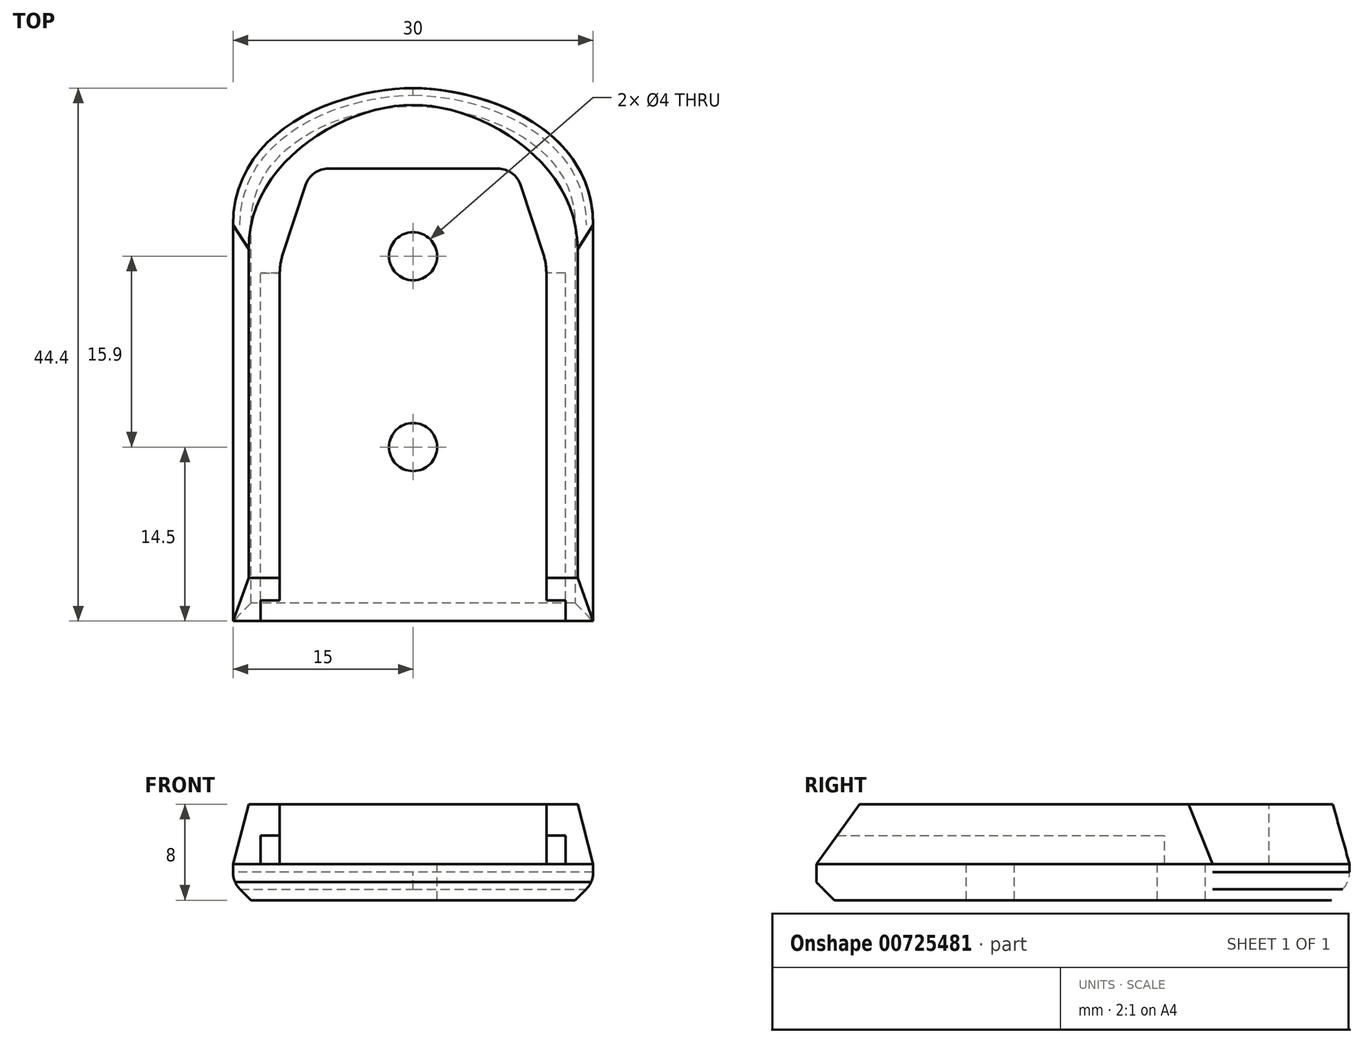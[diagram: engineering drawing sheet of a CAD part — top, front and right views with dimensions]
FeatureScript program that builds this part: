
annotation { "Feature Type Name" : "Feature", "Feature Type Description" : "" }
export const myFeature = defineFeature(function(context is Context, id is Id, definition is map)
    precondition{}
    {
        {
            var Q0;
            Q0=qCreatedBy(makeId("Top.planeOp"),FACE);
            var sketch = newSketch(context, id + "F0", { "sketchPlane" : qUnion([Q0])});
            skLineSegment(sketch, "E0", {"start": v(-15, 0) * mm, "end": v(-15, 33) * mm});
            skFitSpline(sketch, "E1", {"points": [v(-15, 33) * mm, v(0, 44.4) * mm], "startDerivative": vector(0, 25.02) * mm, "endDerivative": vector(16.53, 0) * mm});
            skLineSegment(sketch, "E2", {"start": v(0, 0) * mm, "end": v(-15, 0) * mm});
            skLineSegment(sketch, "E3.MirrorCS", {"start": v(15, 0) * mm, "end": v(15, 33) * mm});
            skLineSegment(sketch, "E4.MirrorCS", {"start": v(0, 0) * mm, "end": v(15, 0) * mm});
            skFitSpline(sketch, "E5.MirrorCS", {"points": [v(15, 33) * mm, v(0, 44.4) * mm], "startDerivative": vector(0, 25.02) * mm, "endDerivative": vector(-16.53, 0) * mm});
            skPoint(sketch, "E6", {"position": v(0, 14.5) * mm});
            skPoint(sketch, "E7", {"position": v(0, 30.4) * mm});
            skLineSegment(sketch, "E8", {"start": v(-11.1, 0) * mm, "end": v(-11.1, 29) * mm});
            skLineSegment(sketch, "E9", {"start": v(-10.85, 30.56) * mm, "end": v(-8.95, 36.33) * mm});
            skLineSegment(sketch, "E10", {"start": v(-7.05, 37.7) * mm, "end": v(0, 37.7) * mm});
            skPoint(sketch, "E11.visualSharp", {"position": v(-11.1, 29.8) * mm});
            skArc(sketch, "E11.filletArc", {"start": v(-10.85, 30.56) * mm, "mid": v(-11.04, 29.8) * mm, "end": v(-11.1, 29) * mm});
            skPoint(sketch, "E12.visualSharp", {"position": v(-8.5, 37.7) * mm});
            skArc(sketch, "E12.filletArc", {"start": v(-7.05, 37.7) * mm, "mid": v(-8.23, 37.32) * mm, "end": v(-8.95, 36.33) * mm});
            skLineSegment(sketch, "E13.MirrorCS", {"start": v(7.05, 37.7) * mm, "end": v(0, 37.7) * mm});
            skArc(sketch, "E14.MirrorCS", {"start": v(7.05, 37.7) * mm, "mid": v(8.23, 37.32) * mm, "end": v(8.95, 36.33) * mm});
            skLineSegment(sketch, "E15.MirrorCS", {"start": v(10.85, 30.56) * mm, "end": v(8.95, 36.33) * mm});
            skArc(sketch, "E16.MirrorCS", {"start": v(10.85, 30.56) * mm, "mid": v(11.04, 29.8) * mm, "end": v(11.1, 29) * mm});
            skLineSegment(sketch, "E17.MirrorCS", {"start": v(11.1, 0) * mm, "end": v(11.1, 29) * mm});
            skSolve(sketch);
        }
        {
            var Q0;
            Q0=makeQuery(id+"F0.imprint","IMPRINT",FACE,{"disambiguationData":[TD([[makeQuery(id+"F0.imprint","IMPRINT",EDGE,{"derivedFrom":sQuery(id+"F0.wireOp",EDGE,"E0")}),-1.0]])]});
            var Q1;
            {var subQ3=sQuery(id+"F0.wireOp",EDGE,"E8");Q1=makeQuery(id+"F0.imprint","IMPRINT",FACE,{"disambiguationData":[TD([[makeQuery(id+"F0.imprint","IMPRINT",EDGE,{"derivedFrom":subQ3}),-1.0]])]});}
            extrude(context, id + "F1", {"entities" : qUnion([Q0, Q1]), "oppositeDirection" : true, "depth" : 3 * mm, "offsetDistance" : 25 * mm});
        }
        {
            var Q0;
            Q0=qCreatedBy(makeId("Top.planeOp"),FACE);
            cPlane(context, id + "F2", {"entities" : qUnion([Q0]), "cplaneType" : CPlaneType.OFFSET, "offset" : 5 * mm, "width" : 150 * mm, "height" : 150 * mm});
        }
        {
            var Q0;
            Q0=qCreatedBy(id+"F2.planeOp",FACE);
            var sketch = newSketch(context, id + "F3", { "sketchPlane" : qUnion([Q0])});
            skLineSegment(sketch, "E18", {"start": v(0, 3.6) * mm, "end": v(-13.7, 3.6) * mm});
            skLineSegment(sketch, "E19", {"start": v(-13.7, 3.6) * mm, "end": v(-13.7, 31) * mm});
            skFitSpline(sketch, "E20", {"points": [v(-13.7, 31) * mm, v(0, 43) * mm], "startDerivative": vector(0, 21.53) * mm, "endDerivative": vector(17.6, 0) * mm});
            skLineSegment(sketch, "E21", {"start": v(-11.1, 3.6) * mm, "end": v(-11.1, 29) * mm});
            skLineSegment(sketch, "E22", {"start": v(-10.85, 30.56) * mm, "end": v(-8.95, 36.33) * mm});
            skLineSegment(sketch, "E23", {"start": v(-7.05, 37.7) * mm, "end": v(0, 37.7) * mm});
            skPoint(sketch, "E24.visualSharp", {"position": v(-11.1, 29.8) * mm});
            skArc(sketch, "E24.filletArc", {"start": v(-10.85, 30.56) * mm, "mid": v(-11.04, 29.8) * mm, "end": v(-11.1, 29) * mm});
            skPoint(sketch, "E25.visualSharp", {"position": v(-8.5, 37.7) * mm});
            skArc(sketch, "E25.filletArc", {"start": v(-7.05, 37.7) * mm, "mid": v(-8.23, 37.32) * mm, "end": v(-8.95, 36.33) * mm});
            skFitSpline(sketch, "E26.MirrorCS", {"points": [v(13.7, 31) * mm, v(0, 43) * mm], "startDerivative": vector(0, 21.53) * mm, "endDerivative": vector(-17.6, 0) * mm});
            skLineSegment(sketch, "E27.MirrorCS", {"start": v(10.85, 30.56) * mm, "end": v(8.95, 36.33) * mm});
            skArc(sketch, "E28.MirrorCS", {"start": v(7.05, 37.7) * mm, "mid": v(8.23, 37.32) * mm, "end": v(8.95, 36.33) * mm});
            skLineSegment(sketch, "E29.MirrorCS", {"start": v(7.05, 37.7) * mm, "end": v(0, 37.7) * mm});
            skArc(sketch, "E30.MirrorCS", {"start": v(10.85, 30.56) * mm, "mid": v(11.04, 29.8) * mm, "end": v(11.1, 29) * mm});
            skLineSegment(sketch, "E31.MirrorCS", {"start": v(11.1, 3.6) * mm, "end": v(11.1, 29) * mm});
            skLineSegment(sketch, "E32.MirrorCS", {"start": v(13.7, 3.6) * mm, "end": v(13.7, 31) * mm});
            skLineSegment(sketch, "E33.MirrorCS", {"start": v(0, 3.6) * mm, "end": v(13.7, 3.6) * mm});
            skSolve(sketch);
        }
        {
            var Q1;
            {var subQ4=sQuery(id+"F0.wireOp",EDGE,"E0");Q1=makeQuery(id+"F0.imprint","IMPRINT",FACE,{"disambiguationData":[TD([[makeQuery(id+"F0.imprint","IMPRINT",EDGE,{"derivedFrom":subQ4}),-1.0]])]});}
            var Q2;
            {var subQ0=sQuery(id+"F3.wireOp",EDGE,"E19");Q2=makeQuery(id+"F3.imprint","IMPRINT",FACE,{"disambiguationData":[TD([[makeQuery(id+"F3.imprint","IMPRINT",EDGE,{"derivedFrom":subQ0}),-1.0]])]});}
            loft(context, id + "F4", {"operationType" : NewBodyOperationType.ADD, "sheetProfilesArray" : [{ "sheetProfileEntities" : qUnion([Q1]) }, { "sheetProfileEntities" : qUnion([Q2]) }]});
        }
        {
            var Q0;
            Q0=sQuery(id+"F0.wireOp",VERTEX,"E7");
            var Q1;
            Q1=sQuery(id+"F0.wireOp",VERTEX,"E6");
            var Q2;
            Q2=makeQuery(id+"F1.opExtrude","SWEPT_BODY",BODY,{"disambiguationData":[OSD([sQuery(id+"F0.wireOp",EDGE,"E0"),sQuery(id+"F0.wireOp",EDGE,"E1"),sQuery(id+"F0.wireOp",EDGE,"E2"),sQuery(id+"F0.wireOp",EDGE,"E3.MirrorCS"),sQuery(id+"F0.wireOp",EDGE,"E4.MirrorCS"),sQuery(id+"F0.wireOp",EDGE,"E5.MirrorCS")])]});
            hole(context, id + "F5", {"style" : HoleStyle.SIMPLE, "endStyle" : HoleEndStyle.BLIND, "holeDiameter" : 4 * mm, "majorDiameter" : 5 * mm, "holeDepth" : 20 * mm, "isTappedThrough" : true, "tappedDepth" : 12 * mm, "tapClearance" : 3, "locations" : qUnion([Q0, Q1]), "scope" : qUnion([Q2])});
        }
        {
            var Q0;
            Q0=makeQuery(id+"F4.opLoft","SWEPT_FACE",FACE,{"disambiguationData":[OSD([sQuery(id+"F0.wireOp",EDGE,"E2"),sQuery(id+"F0.wireOp",EDGE,"E8"),sQuery(id+"F0.wireOp",EDGE,"E11.filletArc"),sQuery(id+"F3.wireOp",EDGE,"E18"),sQuery(id+"F3.wireOp",EDGE,"E21"),sQuery(id+"F3.wireOp",EDGE,"E24.filletArc")])]});
            var sketch = newSketch(context, id + "F6", { "sketchPlane" : qUnion([Q0])});
            skLineSegment(sketch, "E34.bottom", {"start": v(0, 0) * mm, "end": v(29, 0) * mm});
            skLineSegment(sketch, "E34.top", {"start": v(0, 2.4) * mm, "end": v(29, 2.4) * mm});
            skLineSegment(sketch, "E34.left", {"start": v(0, 0) * mm, "end": v(0, 2.4) * mm});
            skLineSegment(sketch, "E34.right", {"start": v(29, 0) * mm, "end": v(29, 2.4) * mm});
            skSolve(sketch);
        }
        {
            var Q0;
            {var subQ0=sQuery(id+"F6.wireOp",EDGE,"E34.bottom");Q0=makeQuery(id+"F6.imprint","IMPRINT",FACE,{"disambiguationData":[TD([[makeQuery(id+"F6.imprint","IMPRINT",EDGE,{"derivedFrom":subQ0}),1.0]])]});}
            var Q1;
            {var subQ0=sQuery(id+"F6.wireOp",EDGE,"E34.right");Q1=makeQuery(id+"F6.imprint","IMPRINT",FACE,{"disambiguationData":[TD([[makeQuery(id+"F6.imprint","IMPRINT",EDGE,{"derivedFrom":subQ0}),1.0]])]});}
            extrude(context, id + "F7", {"entities" : qUnion([Q0, Q1]), "operationType" : NewBodyOperationType.REMOVE, "oppositeDirection" : true, "depth" : 1.6 * mm, "offsetDistance" : 25 * mm});
        }
        {
            var Q0;
            Q0=makeQuery(id+"F4.opLoft","SWEPT_FACE",FACE,{"disambiguationData":[OSD([sQuery(id+"F0.wireOp",EDGE,"E4.MirrorCS"),sQuery(id+"F0.wireOp",EDGE,"E16.MirrorCS"),sQuery(id+"F0.wireOp",EDGE,"E17.MirrorCS"),sQuery(id+"F3.wireOp",EDGE,"E30.MirrorCS"),sQuery(id+"F3.wireOp",EDGE,"E31.MirrorCS"),sQuery(id+"F3.wireOp",EDGE,"E33.MirrorCS")])]});
            var sketch = newSketch(context, id + "F8", { "sketchPlane" : qUnion([Q0])});
            skLineSegment(sketch, "E35.bottom", {"start": v(0, 0) * mm, "end": v(-29, 0) * mm});
            skLineSegment(sketch, "E35.top", {"start": v(0, 2.4) * mm, "end": v(-29, 2.4) * mm});
            skLineSegment(sketch, "E35.left", {"start": v(0, 0) * mm, "end": v(0, 2.4) * mm});
            skLineSegment(sketch, "E35.right", {"start": v(-29, 0) * mm, "end": v(-29, 2.4) * mm});
            skSolve(sketch);
        }
        {
            var Q0;
            {var subQ0=sQuery(id+"F8.wireOp",EDGE,"E35.bottom");Q0=makeQuery(id+"F8.imprint","IMPRINT",FACE,{"disambiguationData":[TD([[makeQuery(id+"F8.imprint","IMPRINT",EDGE,{"derivedFrom":subQ0}),1.0]])]});}
            var Q1;
            {var subQ0=sQuery(id+"F8.wireOp",EDGE,"E35.right");Q1=makeQuery(id+"F8.imprint","IMPRINT",FACE,{"disambiguationData":[TD([[makeQuery(id+"F8.imprint","IMPRINT",EDGE,{"derivedFrom":subQ0}),-1.0]])]});}
            extrude(context, id + "F9", {"entities" : qUnion([Q0, Q1]), "operationType" : NewBodyOperationType.REMOVE, "oppositeDirection" : true, "depth" : 1.6 * mm, "offsetDistance" : 25 * mm});
        }
        {
            var Q0;
            Q0=makeQuery(id+"F1.opExtrude","CAP_EDGE",EDGE,{"disambiguationData":[OSD([sQuery(id+"F0.wireOp",EDGE,"E3.MirrorCS")])],"isStart":false});
            var Q1;
            Q1=makeQuery(id+"F1.opExtrude","CAP_EDGE",EDGE,{"disambiguationData":[OSD([sQuery(id+"F0.wireOp",EDGE,"E2"),sQuery(id+"F0.wireOp",EDGE,"E4.MirrorCS")])],"isStart":false});
            chamfer(context, id + "F10", {"entities" : qUnion([Q0, Q1]), "width" : 1.5 * mm, "tangentPropagation" : true});
        }
        {
            var Q0;
            {var subQ0=sQuery(id+"F0.wireOp",EDGE,"E3.MirrorCS");Q0=makeQuery(id+"F10.opChamfer","BLEND_EDGE",EDGE,{"blendedFrom":[makeQuery(id+"F1.opExtrude","CAP_EDGE",EDGE,{"disambiguationData":[OSD([subQ0])],"isStart":false}),makeQuery(id+"F4.boolean.opBoolean","MERGE",FACE,{"derivedFrom":[makeQuery(id+"F1.opExtrude","SWEPT_FACE",FACE,{"disambiguationData":[OSD([subQ0])]}),makeQuery(id+"F4.opLoft","SWEPT_FACE",FACE,{"disambiguationData":[OSD([subQ0,sQuery(id+"F0.wireOp",EDGE,"E4.MirrorCS"),sQuery(id+"F0.wireOp",EDGE,"E5.MirrorCS"),sQuery(id+"F3.wireOp",EDGE,"E26.MirrorCS"),sQuery(id+"F3.wireOp",EDGE,"E32.MirrorCS"),sQuery(id+"F3.wireOp",EDGE,"E33.MirrorCS")])]})]})],"blendedInto":[makeQuery(id+"F4.boolean.opBoolean","MERGE",FACE,{"derivedFrom":[makeQuery(id+"F1.opExtrude","SWEPT_FACE",FACE,{"disambiguationData":[OSD([subQ0])]}),makeQuery(id+"F4.opLoft","SWEPT_FACE",FACE,{"disambiguationData":[OSD([subQ0,sQuery(id+"F0.wireOp",EDGE,"E4.MirrorCS"),sQuery(id+"F0.wireOp",EDGE,"E5.MirrorCS"),sQuery(id+"F3.wireOp",EDGE,"E26.MirrorCS"),sQuery(id+"F3.wireOp",EDGE,"E32.MirrorCS"),sQuery(id+"F3.wireOp",EDGE,"E33.MirrorCS")])]})]})]});}
            var Q1;
            {var subQ0=sQuery(id+"F0.wireOp",EDGE,"E5.MirrorCS");Q1=makeQuery(id+"F10.opChamfer","BLEND_EDGE",EDGE,{"blendedFrom":[makeQuery(id+"F1.opExtrude","CAP_EDGE",EDGE,{"disambiguationData":[OSD([subQ0])],"isStart":false}),makeQuery(id+"F1.opExtrude","SWEPT_FACE",FACE,{"disambiguationData":[OSD([subQ0])]})],"blendedInto":[makeQuery(id+"F1.opExtrude","SWEPT_FACE",FACE,{"disambiguationData":[OSD([subQ0])]})]});}
            var Q2;
            {var subQ0=sQuery(id+"F0.wireOp",EDGE,"E1");Q2=makeQuery(id+"F10.opChamfer","BLEND_EDGE",EDGE,{"blendedFrom":[makeQuery(id+"F1.opExtrude","CAP_EDGE",EDGE,{"disambiguationData":[OSD([subQ0])],"isStart":false}),makeQuery(id+"F1.opExtrude","SWEPT_FACE",FACE,{"disambiguationData":[OSD([subQ0])]})],"blendedInto":[makeQuery(id+"F1.opExtrude","SWEPT_FACE",FACE,{"disambiguationData":[OSD([subQ0])]})]});}
            fillet(context, id + "F11", {"entities" : qUnion([Q0, Q1, Q2]), "radius" : 2 * mm, "tangentPropagation" : true, "allowEdgeOverflow" : false});
        }
    });
